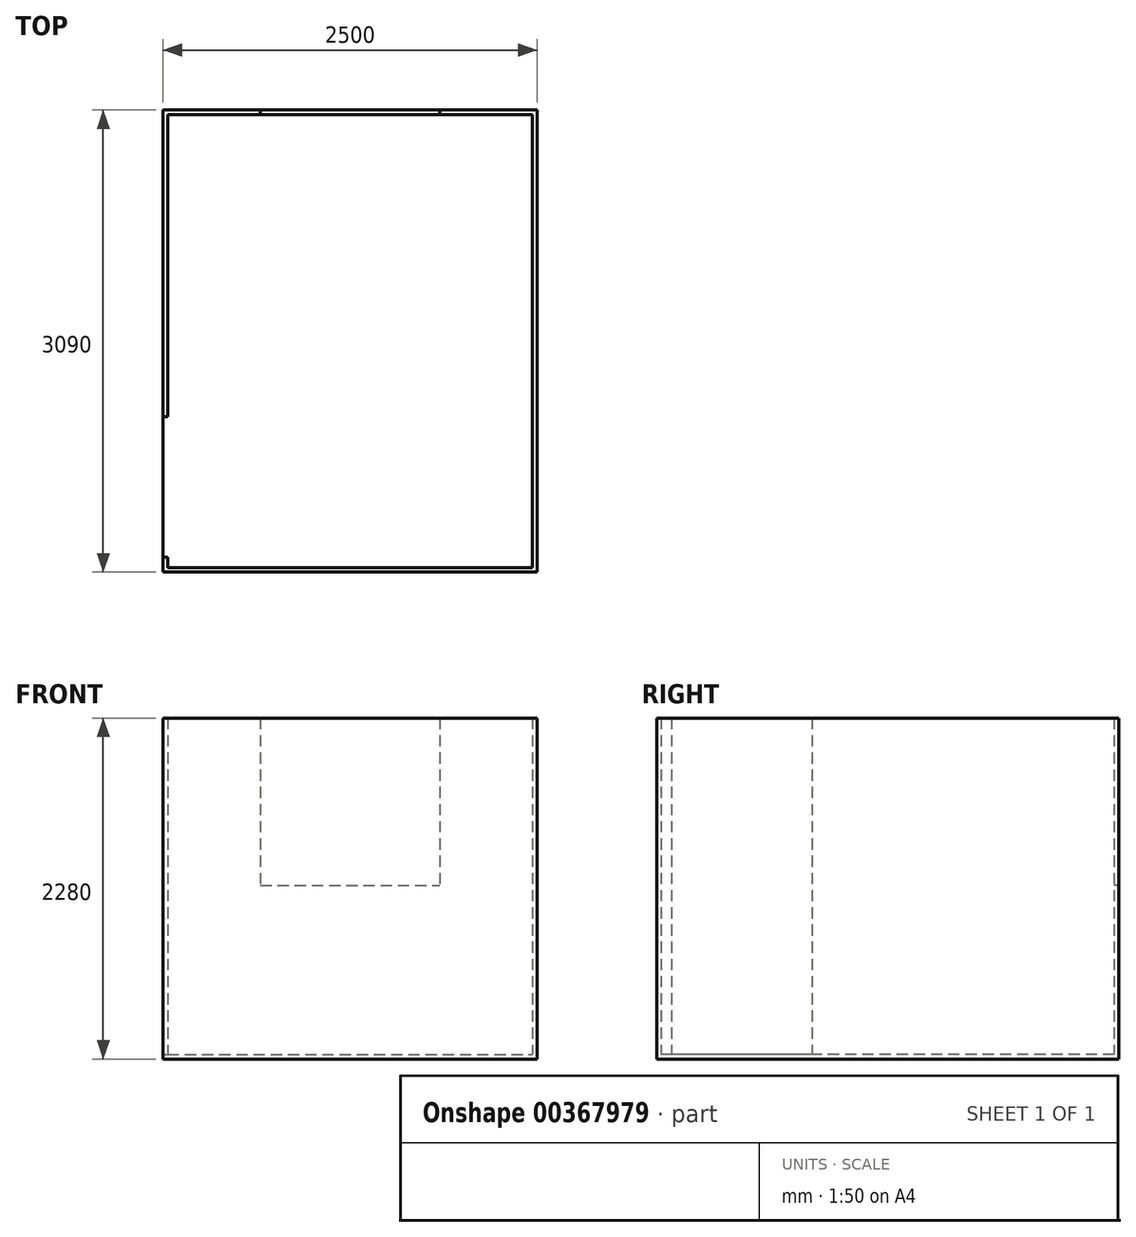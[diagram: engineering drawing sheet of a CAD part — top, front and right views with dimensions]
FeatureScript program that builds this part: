
annotation { "Feature Type Name" : "Feature", "Feature Type Description" : "" }
export const myFeature = defineFeature(function(context is Context, id is Id, definition is map)
    precondition{}
    {
        {
            var Q0;
            Q0=qCreatedBy(makeId("Top.planeOp"),FACE);
            var sketch = newSketch(context, id + "F0", { "sketchPlane" : qUnion([Q0])});
            skLineSegment(sketch, "E0.bottom", {"start": v(0, 3030) * mm, "end": v(2440, 3030) * mm});
            skLineSegment(sketch, "E0.top", {"start": v(0, 0) * mm, "end": v(2440, 0) * mm});
            skLineSegment(sketch, "E0.left", {"start": v(0, 3030) * mm, "end": v(0, 1010) * mm});
            skLineSegment(sketch, "E0.right", {"start": v(2440, 3030) * mm, "end": v(2440, 0) * mm});
            skLineSegment(sketch, "E1.0", {"start": v(-30, 3060) * mm, "end": v(2470, 3060) * mm});
            skLineSegment(sketch, "E1.1", {"start": v(-30, 3060) * mm, "end": v(-30, 1010) * mm});
            skLineSegment(sketch, "E1.2", {"start": v(-30, -30) * mm, "end": v(2470, -30) * mm});
            skLineSegment(sketch, "E1.3", {"start": v(2470, 3060) * mm, "end": v(2470, -30) * mm});
            skLineSegment(sketch, "E2", {"start": v(-30, 1010) * mm, "end": v(0, 1010) * mm});
            skLineSegment(sketch, "E3", {"start": v(-30, 70) * mm, "end": v(0, 70) * mm});
            skLineSegment(sketch, "E4.trimOffspring", {"start": v(-30, 70) * mm, "end": v(-30, -30) * mm});
            skLineSegment(sketch, "E5.trimOffspring", {"start": v(0, 70) * mm, "end": v(0, 0) * mm});
            skSolve(sketch);
        }
        {
            var Q0;
            Q0=makeQuery(id+"F0.imprint","IMPRINT",FACE,{"disambiguationData":[TD([[makeQuery(id+"F0.imprint","IMPRINT",EDGE,{"derivedFrom":sQuery(id+"F0.wireOp",EDGE,"E0.bottom")}),1.0]])]});
            extrude(context, id + "F1", {"entities" : qUnion([Q0]), "depth" : 2250 * mm});
        }
        {
            var Q0;
            Q0=qCreatedBy(makeId("Top.planeOp"),FACE);
            var sketch = newSketch(context, id + "F2", { "sketchPlane" : qUnion([Q0])});
            skLineSegment(sketch, "E6.bottom", {"start": v(2470, 3060) * mm, "end": v(-30, 3060) * mm});
            skLineSegment(sketch, "E6.top", {"start": v(2470, -30) * mm, "end": v(-30, -30) * mm});
            skLineSegment(sketch, "E6.left", {"start": v(2470, 3060) * mm, "end": v(2470, -30) * mm});
            skLineSegment(sketch, "E6.right", {"start": v(-30, 3060) * mm, "end": v(-30, -30) * mm});
            skSolve(sketch);
        }
        {
            var Q0;
            Q0=makeQuery(id+"F2.imprint","IMPRINT",FACE,{"disambiguationData":[TD([[makeQuery(id+"F2.imprint","IMPRINT",EDGE,{"derivedFrom":sQuery(id+"F2.wireOp",EDGE,"E6.bottom")}),1.0]])]});
            extrude(context, id + "F3", {"entities" : qUnion([Q0]), "operationType" : NewBodyOperationType.ADD, "oppositeDirection" : true, "depth" : 30 * mm});
        }
        {
            var Q0;
            Q0=makeQuery(id+"F1.opExtrude","SWEPT_FACE",FACE,{"disambiguationData":[OSD([sQuery(id+"F0.wireOp",EDGE,"E0.bottom")])]});
            var sketch = newSketch(context, id + "F4", { "sketchPlane" : qUnion([Q0])});
            skLineSegment(sketch, "E7.bottom", {"start": v(620, 2250) * mm, "end": v(1820, 2250) * mm});
            skLineSegment(sketch, "E7.top", {"start": v(620, 1130) * mm, "end": v(1820, 1130) * mm});
            skLineSegment(sketch, "E7.left", {"start": v(620, 2250) * mm, "end": v(620, 1130) * mm});
            skLineSegment(sketch, "E7.right", {"start": v(1820, 2250) * mm, "end": v(1820, 1130) * mm});
            skPoint(sketch, "E8", {"position": v(1220, 2250) * mm});
            skSolve(sketch);
        }
        {
            var Q0;
            Q0=makeQuery(id+"F4.imprint","IMPRINT",FACE,{"disambiguationData":[TD([[makeQuery(id+"F4.imprint","IMPRINT",EDGE,{"derivedFrom":sQuery(id+"F4.wireOp",EDGE,"E7.bottom")}),-1.0]])]});
            extrude(context, id + "F5", {"entities" : qUnion([Q0]), "operationType" : NewBodyOperationType.REMOVE, "endBound" : BoundingType.UP_TO_NEXT, "oppositeDirection" : true, "depth" : 25 * mm});
        }
    });
